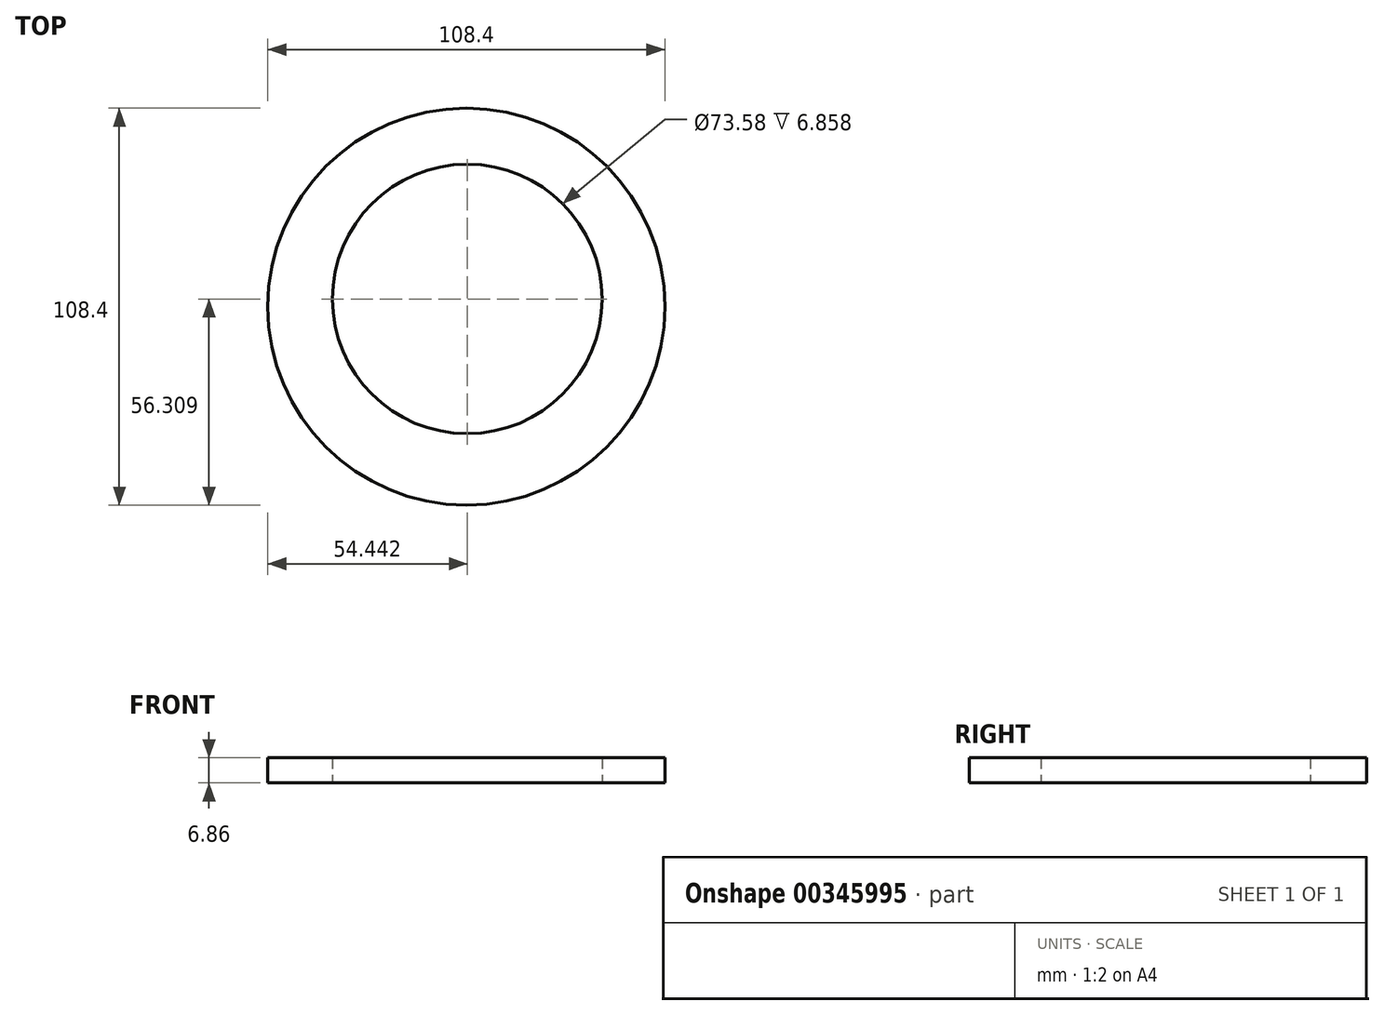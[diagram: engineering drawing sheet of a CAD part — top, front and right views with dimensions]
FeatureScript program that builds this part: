
annotation { "Feature Type Name" : "Feature", "Feature Type Description" : "" }
export const myFeature = defineFeature(function(context is Context, id is Id, definition is map)
    precondition{}
    {
        {
            var Q0;
            Q0=qCreatedBy(makeId("Top.planeOp"),FACE);
            var sketch = newSketch(context, id + "F0", { "sketchPlane" : qUnion([Q0])});
            skPoint(sketch, "E0.0.internal.orphan", {"position": v(0, 44.35) * mm});
            skPoint(sketch, "E0.3.internal.orphan", {"position": v(0, -33.38) * mm});
            skCircle(sketch, "E1", {"center": v(-36.13, 37.4) * mm, "radius": 36.8 * mm});
            skPoint(sketch, "E1.second.point", {"position": v(-72.54, 32.16) * mm});
            skPoint(sketch, "E1.third.point", {"position": v(-53.04, 4.72) * mm});
            skPoint(sketch, "E2.first.point", {"position": v(17.07, 44.35) * mm});
            skPoint(sketch, "E2.second.point", {"position": v(-87.78, 28.5) * mm});
            skPoint(sketch, "E2.third.point", {"position": v(-85.34, 28.5) * mm});
            skCircle(sketch, "E3", {"center": v(-36.37, 35.3) * mm, "radius": 54.2 * mm});
            skPoint(sketch, "E3.second.point", {"position": v(-89.61, 25.15) * mm});
            skPoint(sketch, "E3.third.point", {"position": v(-87.78, 18.14) * mm});
            skSolve(sketch);
        }
        {
            var Q0;
            Q0 = qSketchRegion(id + "F0", true);
            extrude(context, id + "F1", {"entities" : qUnion([Q0]), "depth" : 6.86 * mm});
        }
    });
